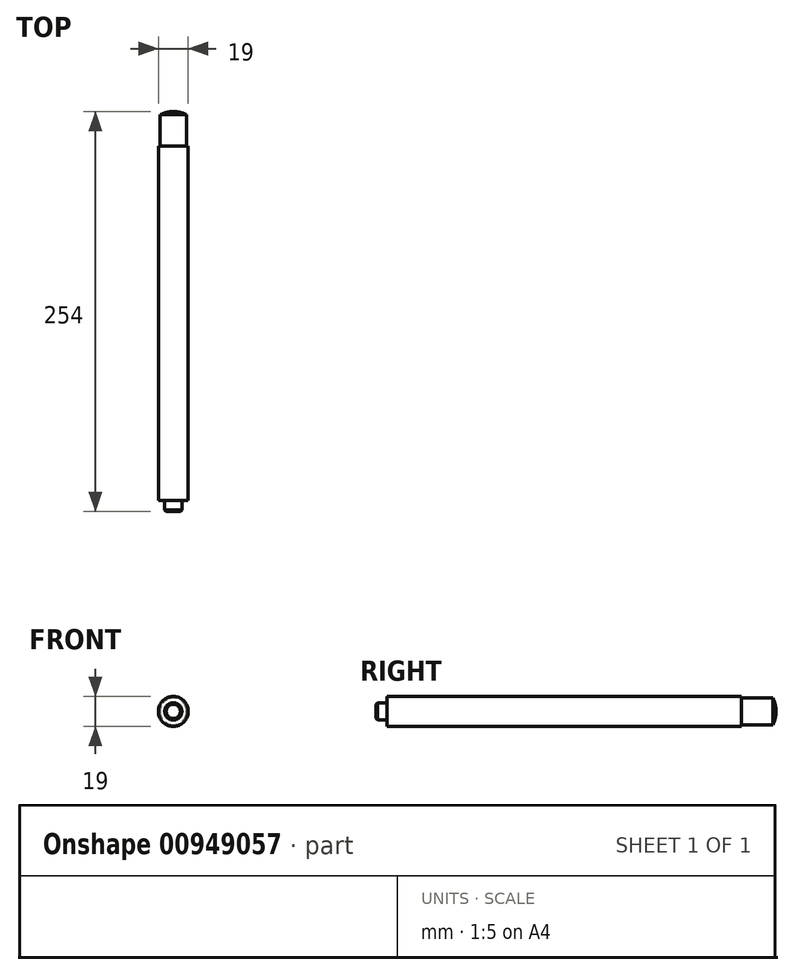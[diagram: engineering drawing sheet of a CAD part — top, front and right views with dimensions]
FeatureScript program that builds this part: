
annotation { "Feature Type Name" : "Feature", "Feature Type Description" : "" }
export const myFeature = defineFeature(function(context is Context, id is Id, definition is map)
    precondition{}
    {
        {
            var Q0;
            Q0=qCreatedBy(makeId("Front.planeOp"),FACE);
            var sketch = newSketch(context, id + "F0", { "sketchPlane" : qUnion([Q0])});
            skCircle(sketch, "E0", {"center": v(0, 0) * mm, "radius": 9.5 * mm});
            skSolve(sketch);
        }
        {
            var Q0;
            Q0 = qSketchRegion(id + "F0", true);
            extrude(context, id + "F1", {"entities" : qUnion([Q0]), "depth" : 225 * mm, "offsetDistance" : 25 * mm});
        }
        {
            var Q0;
            Q0=makeQuery(id+"F1.opExtrude","CAP_FACE",FACE,{"disambiguationData":[OSD([sQuery(id+"F0.wireOp",EDGE,"E0")])],"isStart":false});
            var sketch = newSketch(context, id + "F2", { "sketchPlane" : qUnion([Q0])});
            skCircle(sketch, "E1", {"center": v(0, 0) * mm, "radius": 5.5 * mm});
            skSolve(sketch);
        }
        {
            var Q0;
            Q0 = qSketchRegion(id + "F2", true);
            extrude(context, id + "F3", {"entities" : qUnion([Q0]), "operationType" : NewBodyOperationType.ADD, "depth" : 7 * mm, "offsetDistance" : 25 * mm});
        }
        {
            var Q0;
            Q0=makeQuery(id+"F3.opExtrude","CAP_EDGE",EDGE,{"disambiguationData":[OSD([sQuery(id+"F2.wireOp",EDGE,"E1")])],"isStart":false});
            chamfer(context, id + "F4", {"entities" : qUnion([Q0]), "width" : 1 * mm, "tangentPropagation" : true});
        }
        {
            var Q0;
            Q0=makeQuery(id+"F1.opExtrude","CAP_FACE",FACE,{"disambiguationData":[OSD([sQuery(id+"F0.wireOp",EDGE,"E0")])],"isStart":true});
            var sketch = newSketch(context, id + "F5", { "sketchPlane" : qUnion([Q0])});
            skCircle(sketch, "E2", {"center": v(0, 0) * mm, "radius": 8.5 * mm});
            skSolve(sketch);
        }
        {
            var Q0;
            Q0 = qSketchRegion(id + "F5", true);
            extrude(context, id + "F6", {"entities" : qUnion([Q0]), "operationType" : NewBodyOperationType.ADD, "depth" : 20 * mm, "offsetDistance" : 25 * mm});
        }
        {
            var Q0;
            Q0=qCreatedBy(makeId("Top.planeOp"),FACE);
            var sketch = newSketch(context, id + "F7", { "sketchPlane" : qUnion([Q0])});
            skLineSegment(sketch, "E3", {"start": v(0, 20) * mm, "end": v(0, 0) * mm, "construction": true});
            skLineSegment(sketch, "E4", {"start": v(0, 20) * mm, "end": v(-8.5, 20) * mm});
            skLineSegment(sketch, "E5", {"start": v(0, 20) * mm, "end": v(0, 22) * mm});
            skArc(sketch, "E6", {"start": v(0, 22) * mm, "mid": v(-4.37, 21.5) * mm, "end": v(-8.5, 20) * mm});
            skLineSegment(sketch, "E7", {"start": v(0, 22) * mm, "end": v(-9.65, 22) * mm, "construction": true});
            skSolve(sketch);
        }
        {
            var Q0;
            Q0 = qSketchRegion(id + "F7", true);
            var Q1;
            Q1=sQuery(id+"F7.wireOp",EDGE,"E3");
            revolve(context, id + "F8", {"operationType" : NewBodyOperationType.ADD, "surfaceOperationType" : NewSurfaceOperationType.NEW, "entities" : qUnion([Q0]), "axis" : qUnion([Q1]), "revolveType" : RevolveType.FULL, "oppositeDirection" : true});
        }
    });
